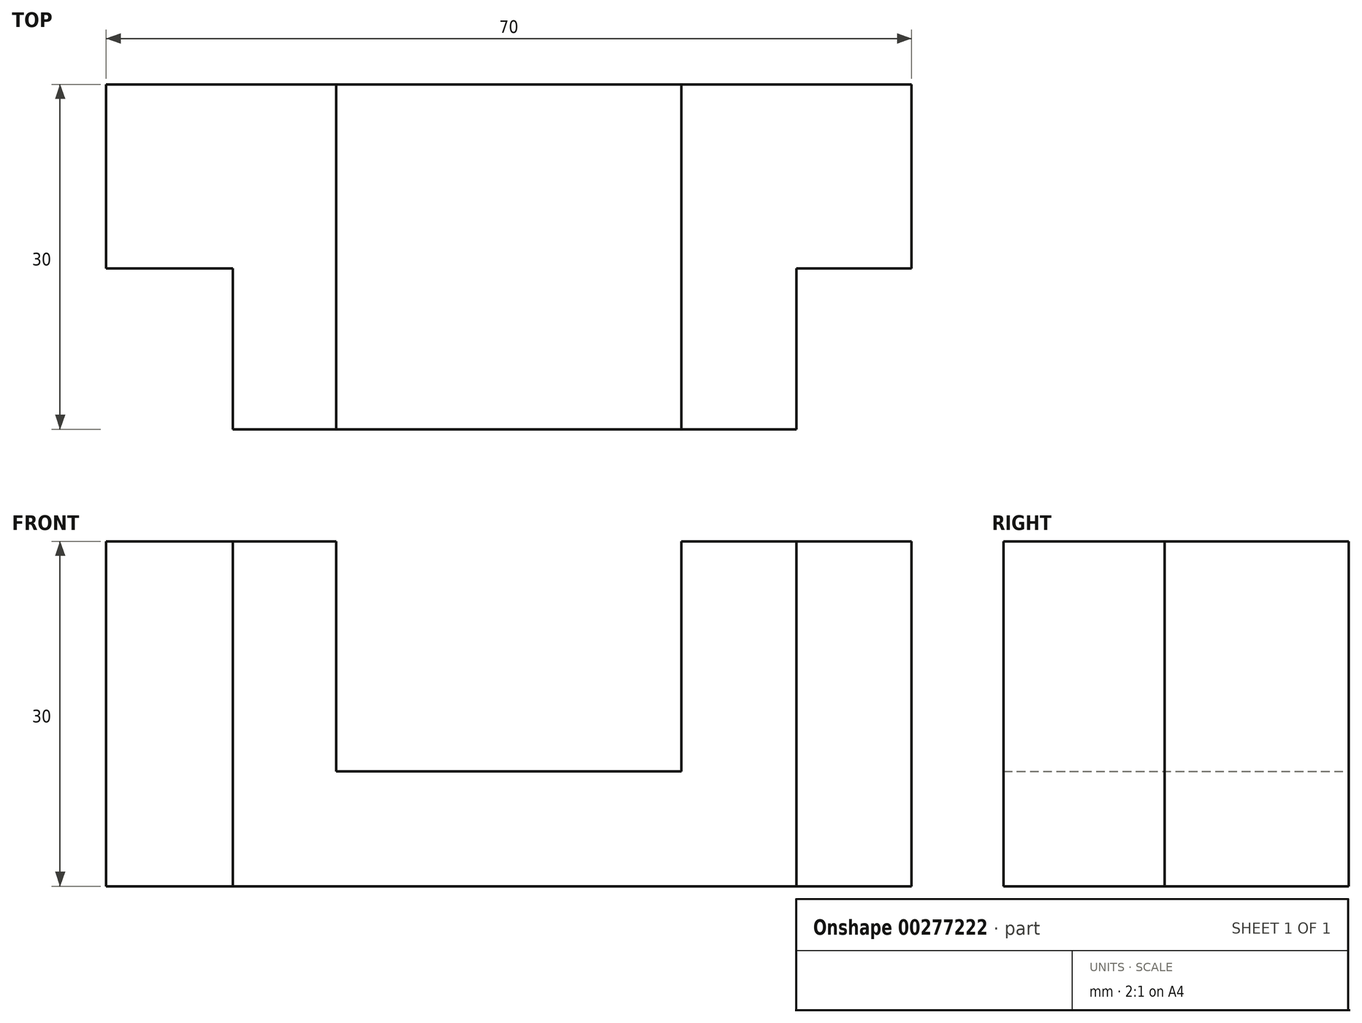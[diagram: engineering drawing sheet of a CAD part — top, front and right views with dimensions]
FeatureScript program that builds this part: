
annotation { "Feature Type Name" : "Feature", "Feature Type Description" : "" }
export const myFeature = defineFeature(function(context is Context, id is Id, definition is map)
    precondition{}
    {
        {
            var Q0;
            Q0=qCreatedBy(makeId("Front.planeOp"),FACE);
            var sketch = newSketch(context, id + "F0", { "sketchPlane" : qUnion([Q0])});
            skLineSegment(sketch, "E0", {"start": v(0, 0) * mm, "end": v(35, 0) * mm});
            skLineSegment(sketch, "E1", {"start": v(35, 0) * mm, "end": v(35, 30) * mm});
            skLineSegment(sketch, "E2", {"start": v(35, 30) * mm, "end": v(15, 30) * mm});
            skLineSegment(sketch, "E3", {"start": v(15, 30) * mm, "end": v(15, 10) * mm});
            skLineSegment(sketch, "E4", {"start": v(15, 10) * mm, "end": v(-15, 10) * mm});
            skLineSegment(sketch, "E5", {"start": v(-15, 10) * mm, "end": v(-15, 30) * mm});
            skLineSegment(sketch, "E6", {"start": v(-15, 30) * mm, "end": v(-35, 30) * mm});
            skLineSegment(sketch, "E7", {"start": v(-35, 30) * mm, "end": v(-35, 0) * mm});
            skLineSegment(sketch, "E8", {"start": v(-35, 0) * mm, "end": v(0, 0) * mm});
            skLineSegment(sketch, "E9", {"start": v(-35, 30) * mm, "end": v(-24, 30) * mm});
            skLineSegment(sketch, "E10", {"start": v(-24, 30) * mm, "end": v(-24, 0) * mm});
            skLineSegment(sketch, "E11", {"start": v(-24, 0) * mm, "end": v(0, 0) * mm});
            skLineSegment(sketch, "E12", {"start": v(15, 30) * mm, "end": v(25, 30) * mm});
            skLineSegment(sketch, "E13", {"start": v(25, 30) * mm, "end": v(25, 0) * mm});
            skLineSegment(sketch, "E14", {"start": v(25, 0) * mm, "end": v(0, 0) * mm});
            skSolve(sketch);
        }
        {
            var Q0;
            Q0=makeQuery(id+"F0.imprint","IMPRINT",FACE,{"disambiguationData":[TD([[makeQuery(id+"F0.imprint","IMPRINT",EDGE,{"derivedFrom":sQuery(id+"F0.wireOp",EDGE,"E3")}),1.0]])]});
            extrude(context, id + "F1", {"entities" : qUnion([Q0]), "depth" : 30 * mm});
        }
        {
            var Q0;
            Q0 = qSketchRegion(id + "F0", true);
            extrude(context, id + "F2", {"entities" : qUnion([Q0]), "operationType" : NewBodyOperationType.ADD, "depth" : 16 * mm});
        }
    });
